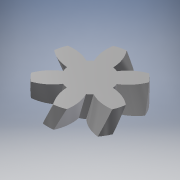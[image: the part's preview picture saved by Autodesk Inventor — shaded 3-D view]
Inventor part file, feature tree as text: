
AUTODESK INVENTOR PART (.ipt)
format: ipt  version: 2017 SP1 (Build 210196100, 196)  size: 240,640 bytes
history: native  units: mm (DEFAULTED — no unit token found)
features: plane x3, other x3, sketch x3, extrude x2
ambient origin geometry x8: Origin, YZ Plane, XZ Plane, XY Plane, X Axis, Y Axis, Z Axis, Center Point
bodies: Solid1 (feature_tree)
feature tree (11):
  extrude  "Extrusion1"  Depth=10.0mm TaperAngle=0.0deg
  plane  "Work Plane2"
  plane  "Work Plane8"
  plane  "Work Plane9"
  other  "Engrenage cylindrique"
  extrude  "Extrusion2"  Depth=10.0mm TaperAngle=0.0deg
  sketch  "Sketch1"  dims[d0=38.885336mm d1=10.0mm d2=0.0mm]
  sketch  "Sketch2"  dims[d3=30.066593mm d4=10.0mm d5=0.0mm d16=30.066593mm d17=0.0mm d34=30.0deg d39=0.0mm d41=0.0mm d43=30.066593mm d46=30.066593mm d47=0.0mm d48=0.0mm d49=5.0mm d50=10.0mm d51=0.0mm]
  other  "Srf1"
  sketch  "Esquisse3"
  other  "Diamètre primitif"
